# Revit family: 210_629dc5ef25c84ebdb10924750c8099
name_source: partatom
category: Mechanical Equipment
revit_build: Autodesk Revit 2018 (Build: 20170223_1515(x64)
units: mm (PartAtom-declared; Revit-internal decimal feet)

## family parameters
Always vertical = Yes
Cut with Voids When Loaded = No
Part Type = Breaks Into
Room Calculation Point = No
Round Connector Dimension = Use Diameter
Shared = No
Work Plane-Based = No

## types (5) — shared parameters
CAT0 = Yes
Description = DTH roof fan with horizontal exhaust
Manufacturer = Exhausto
QmdConnectorList = 201;D
TH = 5 mm  [stored 0.0164042 ft]
W = 500 mm
magiPartTypeId = 210
magiProductFamilyId = 629dc5ef25c84ebdb10924750c8099

## per-type parameters (varying)
| type | BDD | BLL | D | H11 | H2 | H22 | H3 | X1 | X2 | X3 | X4 | magiProductId |
| DTH160-4-1 | 138 mm | 110 mm  [stored 0.360892 ft] | 160 mm | 57 mm | 90 mm | 36 mm | 67 mm | 152 mm | 145 mm  [stored 0.475722 ft] | 96 mm | 128 mm | 72a85d406a8e4d06a210da9a1e2a0a |
| DTH400-4-1EC | 306 mm | 230 mm  [stored 0.754593 ft] | 400 mm | 106 mm | 167 mm | 67 mm | 116 mm | 337 mm | 323 mm | 213 mm | 284 mm | d5ce42f967a8487e889c0ff10f2d1c |
| DTH315-4-1EC | 261 mm | 188 mm | 315 mm | 95 mm | 150 mm | 60 mm | 105 mm | 287 mm | 275 mm | 182 mm | 242 mm | 2b0fe08014a94c58bbdc2eacf30d09 |
| DTH250-4-1EC | 221 mm | 155 mm  [stored 0.50853 ft] | 250 mm | 83 mm | 130 mm  [stored 0.426509 ft] | 52 mm | 93 mm | 243 mm | 233 mm | 153 mm | 205 mm | 863888adadde43f5be9bd134dc53d4 |
| DTH200-4-1 | 173 mm | 130 mm  [stored 0.426509 ft] | 200 mm | 66 mm | 103 mm | 41 mm | 76 mm | 191 mm | 183 mm | 120 mm | 161 mm | 8baa0bcaaceb41c9b9b40e227c4bc4 |

note: column(s) folded — value = type name in every type: MC Product Code

note: [stored X ft] marks values corroborated as IEEE doubles in the binary element streams (Revit-internal decimal feet)

## geometry (parser evidence)
native form markers: Sweep x3
no freeform markers — native parametric forms only
